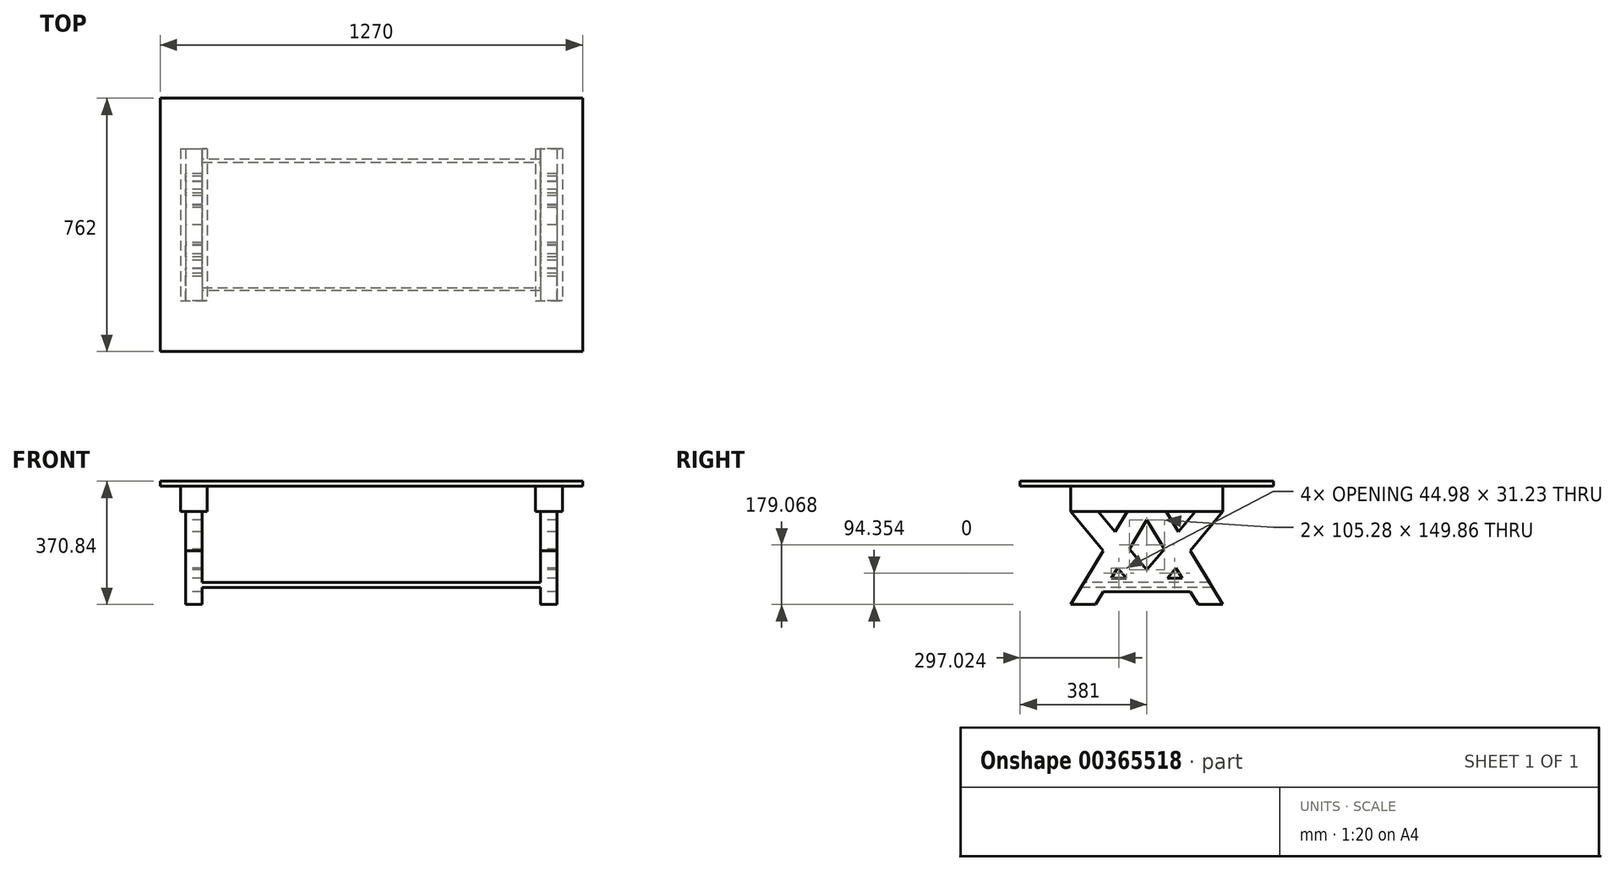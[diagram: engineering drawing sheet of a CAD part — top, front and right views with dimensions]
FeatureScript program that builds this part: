
annotation { "Feature Type Name" : "Feature", "Feature Type Description" : "" }
export const myFeature = defineFeature(function(context is Context, id is Id, definition is map)
    precondition{}
    {
        {
            var Q0;
            Q0=qCreatedBy(makeId("Front.planeOp"),FACE);
            var sketch = newSketch(context, id + "F0", { "sketchPlane" : qUnion([Q0])});
            skLineSegment(sketch, "E0.bottom", {"start": v(-1121.29, 22.04) * mm, "end": v(148.71, 22.04) * mm});
            skLineSegment(sketch, "E0.top", {"start": v(-1121.29, 6.8) * mm, "end": v(148.71, 6.8) * mm});
            skLineSegment(sketch, "E0.left", {"start": v(-1121.29, 22.04) * mm, "end": v(-1121.29, 6.8) * mm});
            skLineSegment(sketch, "E0.right", {"start": v(148.71, 22.04) * mm, "end": v(148.71, 6.8) * mm});
            skLineSegment(sketch, "E1", {"start": v(-1045.09, -69.4) * mm, "end": v(-1045.09, -348.8) * mm});
            skLineSegment(sketch, "E2", {"start": v(-1045.09, -348.8) * mm, "end": v(-994.29, -348.8) * mm});
            skLineSegment(sketch, "E3", {"start": v(-994.29, -348.8) * mm, "end": v(-994.29, -69.4) * mm});
            skLineSegment(sketch, "E4", {"start": v(-486.29, 6.8) * mm, "end": v(-486.29, -279.71) * mm, "construction": true});
            skLineSegment(sketch, "E5", {"start": v(-994.29, -298) * mm, "end": v(-486.29, -298) * mm});
            skLineSegment(sketch, "E6.0", {"start": v(-994.29, -282.76) * mm, "end": v(-486.29, -282.76) * mm});
            skLineSegment(sketch, "E7", {"start": v(-1060.33, 6.8) * mm, "end": v(-1060.33, -69.4) * mm});
            skLineSegment(sketch, "E8", {"start": v(-1060.33, -69.4) * mm, "end": v(-1045.09, -69.4) * mm});
            skLineSegment(sketch, "E9", {"start": v(-979.05, 6.8) * mm, "end": v(-979.05, -69.4) * mm});
            skLineSegment(sketch, "E10", {"start": v(-979.05, -69.4) * mm, "end": v(-994.29, -69.4) * mm});
            skLineSegment(sketch, "E11", {"start": v(-979.05, -69.4) * mm, "end": v(-940.95, -69.4) * mm});
            skLineSegment(sketch, "E12", {"start": v(-994.29, -82.1) * mm, "end": v(-486.29, -82.1) * mm});
            skLineSegment(sketch, "E13.0", {"start": v(-928.25, 6.8) * mm, "end": v(-928.25, -69.4) * mm});
            skLineSegment(sketch, "E14.0", {"start": v(-623.45, 6.8) * mm, "end": v(-623.45, -5.9) * mm});
            skLineSegment(sketch, "E15.0", {"start": v(-610.75, 6.8) * mm, "end": v(-610.75, -5.9) * mm});
            skLineSegment(sketch, "E16.0", {"start": v(-921.9, -5.9) * mm, "end": v(-921.9, -18.6) * mm});
            skLineSegment(sketch, "E17.0", {"start": v(-629.8, -5.9) * mm, "end": v(-629.8, -18.6) * mm});
            skLineSegment(sketch, "E18.0", {"start": v(-604.4, -5.9) * mm, "end": v(-604.4, -18.6) * mm});
            skLineSegment(sketch, "E19", {"start": v(-928.25, -18.6) * mm, "end": v(-623.45, -18.6) * mm});
            skLineSegment(sketch, "E20.0", {"start": v(-928.25, -5.9) * mm, "end": v(-623.45, -5.9) * mm});
            skLineSegment(sketch, "E21.trimOffspring", {"start": v(-623.45, -18.6) * mm, "end": v(-623.45, -69.4) * mm});
            skLineSegment(sketch, "E22.trimOffspring", {"start": v(-610.75, -18.6) * mm, "end": v(-610.75, -69.4) * mm});
            skLineSegment(sketch, "E23.trimOffspring", {"start": v(-610.75, -5.9) * mm, "end": v(-604.4, -5.9) * mm});
            skLineSegment(sketch, "E24.trimOffspring", {"start": v(-610.75, -18.6) * mm, "end": v(-604.4, -18.6) * mm});
            skLineSegment(sketch, "E25.trimOffspring", {"start": v(-610.75, -69.4) * mm, "end": v(-486.29, -69.4) * mm});
            skLineSegment(sketch, "E26.0", {"start": v(-940.95, 6.8) * mm, "end": v(-940.95, -69.4) * mm});
            skLineSegment(sketch, "E27.trimOffspring", {"start": v(-928.25, -69.4) * mm, "end": v(-623.45, -69.4) * mm});
            skPoint(sketch, "E28.orphan", {"position": v(-1045.09, 6.8) * mm});
            skLineSegment(sketch, "E29.MirrorCS", {"start": v(-361.83, -69.4) * mm, "end": v(-486.29, -69.4) * mm});
            skLineSegment(sketch, "E30.MirrorCS", {"start": v(21.71, -82.1) * mm, "end": v(-486.29, -82.1) * mm});
            skLineSegment(sketch, "E31.MirrorCS", {"start": v(-361.83, -18.6) * mm, "end": v(-361.83, -69.4) * mm});
            skLineSegment(sketch, "E32.MirrorCS", {"start": v(-349.13, -18.6) * mm, "end": v(-349.13, -69.4) * mm});
            skLineSegment(sketch, "E33.MirrorCS", {"start": v(-44.33, -18.6) * mm, "end": v(-349.13, -18.6) * mm});
            skLineSegment(sketch, "E34.MirrorCS", {"start": v(-342.78, -5.9) * mm, "end": v(-342.78, -18.6) * mm});
            skLineSegment(sketch, "E35.MirrorCS", {"start": v(-44.33, -5.9) * mm, "end": v(-349.13, -5.9) * mm});
            skLineSegment(sketch, "E36.MirrorCS", {"start": v(-361.83, -5.9) * mm, "end": v(-368.18, -5.9) * mm});
            skLineSegment(sketch, "E37.MirrorCS", {"start": v(-368.18, -5.9) * mm, "end": v(-368.18, -18.6) * mm});
            skLineSegment(sketch, "E38.MirrorCS", {"start": v(-361.83, -18.6) * mm, "end": v(-368.18, -18.6) * mm});
            skLineSegment(sketch, "E39.MirrorCS", {"start": v(-361.83, 6.8) * mm, "end": v(-361.83, -5.9) * mm});
            skLineSegment(sketch, "E40.MirrorCS", {"start": v(-349.13, 6.8) * mm, "end": v(-349.13, -5.9) * mm});
            skLineSegment(sketch, "E41.MirrorCS", {"start": v(-44.33, -69.4) * mm, "end": v(-349.13, -69.4) * mm});
            skLineSegment(sketch, "E42.MirrorCS", {"start": v(-44.33, 6.8) * mm, "end": v(-44.33, -69.4) * mm});
            skLineSegment(sketch, "E43.MirrorCS", {"start": v(-50.68, -5.9) * mm, "end": v(-50.68, -18.6) * mm});
            skLineSegment(sketch, "E44.MirrorCS", {"start": v(-31.63, 6.8) * mm, "end": v(-31.63, -69.4) * mm});
            skLineSegment(sketch, "E45.MirrorCS", {"start": v(6.47, 6.8) * mm, "end": v(6.47, -69.4) * mm});
            skLineSegment(sketch, "E46.MirrorCS", {"start": v(87.75, 6.8) * mm, "end": v(87.75, -69.4) * mm});
            skLineSegment(sketch, "E47.MirrorCS", {"start": v(87.75, -69.4) * mm, "end": v(72.51, -69.4) * mm});
            skLineSegment(sketch, "E48.MirrorCS", {"start": v(6.47, -69.4) * mm, "end": v(21.71, -69.4) * mm});
            skLineSegment(sketch, "E49.MirrorCS", {"start": v(21.71, -348.8) * mm, "end": v(21.71, -69.4) * mm});
            skLineSegment(sketch, "E50.MirrorCS", {"start": v(72.51, -69.4) * mm, "end": v(72.51, -348.8) * mm});
            skLineSegment(sketch, "E51.MirrorCS", {"start": v(72.51, -348.8) * mm, "end": v(21.71, -348.8) * mm});
            skLineSegment(sketch, "E52.MirrorCS", {"start": v(21.71, -282.76) * mm, "end": v(-486.29, -282.76) * mm});
            skLineSegment(sketch, "E53.MirrorCS", {"start": v(21.71, -298) * mm, "end": v(-486.29, -298) * mm});
            skSolve(sketch);
        }
        {
            var Q0;
            Q0=makeQuery(id+"F0.imprint","IMPRINT",FACE,{"disambiguationData":[TD([[makeQuery(id+"F0.imprint","IMPRINT",EDGE,{"derivedFrom":sQuery(id+"F0.wireOp",EDGE,"E0.bottom")}),-1.0]])]});
            extrude(context, id + "F1", {"entities" : qUnion([Q0]), "oppositeDirection" : true, "depth" : 609.6 * mm, "hasSecondDirection" : true, "secondDirectionOppositeDirection" : false, "secondDirectionDepth" : 152.4 * mm});
        }
        {
            var Q0;
            Q0=makeQuery(id+"F0.imprint","IMPRINT",FACE,{"disambiguationData":[TD([[makeQuery(id+"F0.imprint","IMPRINT",EDGE,{"derivedFrom":sQuery(id+"F0.wireOp",EDGE,"E1")}),1.0]])]});
            var Q1;
            {var subQ6=sQuery(id+"F0.wireOp",EDGE,"E45.MirrorCS");Q1=makeQuery(id+"F0.imprint","IMPRINT",FACE,{"disambiguationData":[TD([[makeQuery(id+"F0.imprint","IMPRINT",EDGE,{"derivedFrom":subQ6}),1.0]])]});}
            extrude(context, id + "F2", {"entities" : qUnion([Q0, Q1]), "operationType" : NewBodyOperationType.ADD, "oppositeDirection" : true, "depth" : 457.2 * mm});
        }
        {
            var Q0;
            {var subQ4=sQuery(id+"F0.wireOp",EDGE,"E5");Q0=makeQuery(id+"F0.imprint","IMPRINT",FACE,{"disambiguationData":[TD([[makeQuery(id+"F0.imprint","IMPRINT",EDGE,{"derivedFrom":subQ4}),1.0]])]});}
            extrude(context, id + "F3", {"entities" : qUnion([Q0]), "operationType" : NewBodyOperationType.ADD, "oppositeDirection" : true, "depth" : 457.2 * mm});
        }
        {
            var Q0;
            Q0=makeQuery(id+"F2.opExtrude","SWEPT_FACE",FACE,{"disambiguationData":[OSD([sQuery(id+"F0.wireOp",EDGE,"E7")])]});
            var sketch = newSketch(context, id + "F4", { "sketchPlane" : qUnion([Q0])});
            skLineSegment(sketch, "E54.0", {"start": v(-457.2, -348.8) * mm, "end": v(0, -348.8) * mm});
            skLineSegment(sketch, "E55", {"start": v(-228.6, 6.8) * mm, "end": v(-228.6, -348.8) * mm, "construction": true});
            skLineSegment(sketch, "E56.0", {"start": v(-457.2, -298) * mm, "end": v(0, -298) * mm, "construction": true});
            skLineSegment(sketch, "E57.0", {"start": v(-457.2, -282.76) * mm, "end": v(0, -282.76) * mm, "construction": true});
            skLineSegment(sketch, "E58.0", {"start": v(-457.2, -270.06) * mm, "end": v(0, -270.06) * mm});
            skLineSegment(sketch, "E59.0", {"start": v(-457.2, -310.7) * mm, "end": v(0, -310.7) * mm});
            skLineSegment(sketch, "E60", {"start": v(-457.2, -69.4) * mm, "end": v(-290.08, -270.06) * mm});
            skLineSegment(sketch, "E61", {"start": v(-374.56, -69.4) * mm, "end": v(-228.6, -244.66) * mm});
            skLineSegment(sketch, "E62", {"start": v(-457.2, -348.8) * mm, "end": v(-287.47, -69.4) * mm});
            skLineSegment(sketch, "E63", {"start": v(-228.6, -94.8) * mm, "end": v(-382.9, -348.8) * mm});
            skLineSegment(sketch, "E64", {"start": v(-228.6, -244.66) * mm, "end": v(-82.64, -69.4) * mm});
            skLineSegment(sketch, "E65", {"start": v(0, -69.4) * mm, "end": v(-167.12, -270.06) * mm});
            skLineSegment(sketch, "E66", {"start": v(-228.6, -94.8) * mm, "end": v(-74.3, -348.8) * mm});
            skLineSegment(sketch, "E67", {"start": v(0, -348.8) * mm, "end": v(-169.73, -69.4) * mm});
            skLineSegment(sketch, "E68.0", {"start": v(0, -69.4) * mm, "end": v(0, -348.8) * mm});
            skLineSegment(sketch, "E68.1", {"start": v(-457.2, -69.4) * mm, "end": v(-457.2, -348.8) * mm});
            skSolve(sketch);
        }
        {
            var Q0;
            {var subQ0=sQuery(id+"F4.wireOp",EDGE,"E68.1");var subQ1=sQuery(id+"F4.wireOp",EDGE,"E58.0");var subQ2=makeQuery(id+"F4.imprint","INTERSECT",VERTEX,{"derivedFrom":[subQ1,subQ0]});Q0=makeQuery(id+"F4.imprint","IMPRINT",FACE,{"disambiguationData":[TD([[makeQuery(id+"F4.imprint","IMPRINT",EDGE,{"disambiguationData":[TD([[subQ2,-1.0]])],"derivedFrom":subQ1}),1.0]])]});}
            var Q1;
            {var subQ0=sQuery(id+"F4.wireOp",EDGE,"E61");var subQ3=sQuery(id+"F4.wireOp",EDGE,"E62");var subQ4=makeQuery(id+"F4.imprint","INTERSECT",VERTEX,{"derivedFrom":[subQ0,subQ3]});Q1=makeQuery(id+"F4.imprint","IMPRINT",FACE,{"disambiguationData":[TD([[makeQuery(id+"F4.imprint","IMPRINT",EDGE,{"disambiguationData":[TD([[subQ4,1.0]])],"derivedFrom":subQ0}),1.0]])]});}
            var Q2;
            {var subQ0=sQuery(id+"F4.wireOp",EDGE,"E64");var subQ1=sQuery(id+"F4.wireOp",EDGE,"E61");var subQ2=makeQuery(id+"F4.imprint","INTERSECT",VERTEX,{"derivedFrom":[subQ1,subQ0]});Q2=makeQuery(id+"F4.imprint","IMPRINT",FACE,{"disambiguationData":[TD([[makeQuery(id+"F4.imprint","IMPRINT",EDGE,{"disambiguationData":[TD([[subQ2,1.0]])],"derivedFrom":subQ1}),1.0]])]});}
            var Q3;
            {var subQ0=sQuery(id+"F4.wireOp",EDGE,"E64");var subQ3=sQuery(id+"F4.wireOp",EDGE,"E67");var subQ4=makeQuery(id+"F4.imprint","INTERSECT",VERTEX,{"derivedFrom":[subQ0,subQ3]});Q3=makeQuery(id+"F4.imprint","IMPRINT",FACE,{"disambiguationData":[TD([[makeQuery(id+"F4.imprint","IMPRINT",EDGE,{"disambiguationData":[TD([[subQ4,-1.0]])],"derivedFrom":subQ0}),1.0]])]});}
            var Q4;
            {var subQ0=sQuery(id+"F4.wireOp",EDGE,"E68.0");var subQ1=sQuery(id+"F4.wireOp",EDGE,"E58.0");var subQ2=makeQuery(id+"F4.imprint","INTERSECT",VERTEX,{"derivedFrom":[subQ1,subQ0]});Q4=makeQuery(id+"F4.imprint","IMPRINT",FACE,{"disambiguationData":[TD([[makeQuery(id+"F4.imprint","IMPRINT",EDGE,{"disambiguationData":[TD([[subQ2,1.0]])],"derivedFrom":subQ1}),1.0]])]});}
            var Q5;
            {var subQ0=sQuery(id+"F4.wireOp",EDGE,"E65");var subQ1=sQuery(id+"F4.wireOp",EDGE,"E58.0");var subQ2=makeQuery(id+"F4.imprint","INTERSECT",VERTEX,{"derivedFrom":[subQ1,subQ0]});Q5=makeQuery(id+"F4.imprint","IMPRINT",FACE,{"disambiguationData":[TD([[makeQuery(id+"F4.imprint","IMPRINT",EDGE,{"disambiguationData":[TD([[subQ2,-1.0]])],"derivedFrom":subQ1}),1.0]])]});}
            var Q6;
            {var subQ0=sQuery(id+"F4.wireOp",EDGE,"E60");var subQ1=sQuery(id+"F4.wireOp",EDGE,"E58.0");var subQ2=makeQuery(id+"F4.imprint","INTERSECT",VERTEX,{"derivedFrom":[subQ1,subQ0]});Q6=makeQuery(id+"F4.imprint","IMPRINT",FACE,{"disambiguationData":[TD([[makeQuery(id+"F4.imprint","IMPRINT",EDGE,{"disambiguationData":[TD([[subQ2,1.0]])],"derivedFrom":subQ1}),1.0]])]});}
            var Q7;
            {var subQ0=sQuery(id+"F4.wireOp",EDGE,"E63");var subQ1=sQuery(id+"F4.wireOp",EDGE,"E54.0");var subQ2=makeQuery(id+"F4.imprint","INTERSECT",VERTEX,{"derivedFrom":[subQ1,subQ0]});Q7=makeQuery(id+"F4.imprint","IMPRINT",FACE,{"disambiguationData":[TD([[makeQuery(id+"F4.imprint","IMPRINT",EDGE,{"disambiguationData":[TD([[subQ2,-1.0]])],"derivedFrom":subQ1}),1.0]])]});}
            var Q8;
            {var subQ0=sQuery(id+"F4.wireOp",EDGE,"E68.1");var subQ1=sQuery(id+"F4.wireOp",EDGE,"E59.0");var subQ2=makeQuery(id+"F4.imprint","INTERSECT",VERTEX,{"derivedFrom":[subQ1,subQ0]});Q8=makeQuery(id+"F4.imprint","IMPRINT",FACE,{"disambiguationData":[TD([[makeQuery(id+"F4.imprint","IMPRINT",EDGE,{"disambiguationData":[TD([[subQ2,-1.0]])],"derivedFrom":subQ1}),-1.0]])]});}
            var Q9;
            {var subQ0=sQuery(id+"F4.wireOp",EDGE,"E68.0");var subQ1=sQuery(id+"F4.wireOp",EDGE,"E59.0");var subQ2=makeQuery(id+"F4.imprint","INTERSECT",VERTEX,{"derivedFrom":[subQ1,subQ0]});Q9=makeQuery(id+"F4.imprint","IMPRINT",FACE,{"disambiguationData":[TD([[makeQuery(id+"F4.imprint","IMPRINT",EDGE,{"disambiguationData":[TD([[subQ2,1.0]])],"derivedFrom":subQ1}),-1.0]])]});}
            var Q10;
            {var subQ0=sQuery(id+"F4.wireOp",EDGE,"E68.0");var subQ1=sQuery(id+"F4.wireOp",EDGE,"E58.0");var subQ2=makeQuery(id+"F4.imprint","INTERSECT",VERTEX,{"derivedFrom":[subQ1,subQ0]});Q10=makeQuery(id+"F4.imprint","IMPRINT",FACE,{"disambiguationData":[TD([[makeQuery(id+"F4.imprint","IMPRINT",EDGE,{"disambiguationData":[TD([[subQ2,1.0]])],"derivedFrom":subQ1}),-1.0]])]});}
            var Q11;
            {var subQ0=sQuery(id+"F4.wireOp",EDGE,"E68.1");var subQ1=sQuery(id+"F4.wireOp",EDGE,"E58.0");var subQ2=makeQuery(id+"F4.imprint","INTERSECT",VERTEX,{"derivedFrom":[subQ1,subQ0]});Q11=makeQuery(id+"F4.imprint","IMPRINT",FACE,{"disambiguationData":[TD([[makeQuery(id+"F4.imprint","IMPRINT",EDGE,{"disambiguationData":[TD([[subQ2,-1.0]])],"derivedFrom":subQ1}),-1.0]])]});}
            extrude(context, id + "F5", {"entities" : qUnion([Q0, Q1, Q2, Q3, Q4, Q5, Q6, Q7, Q8, Q9, Q10, Q11]), "operationType" : NewBodyOperationType.REMOVE, "oppositeDirection" : true, "depth" : 2540 * mm});
        }
    });
